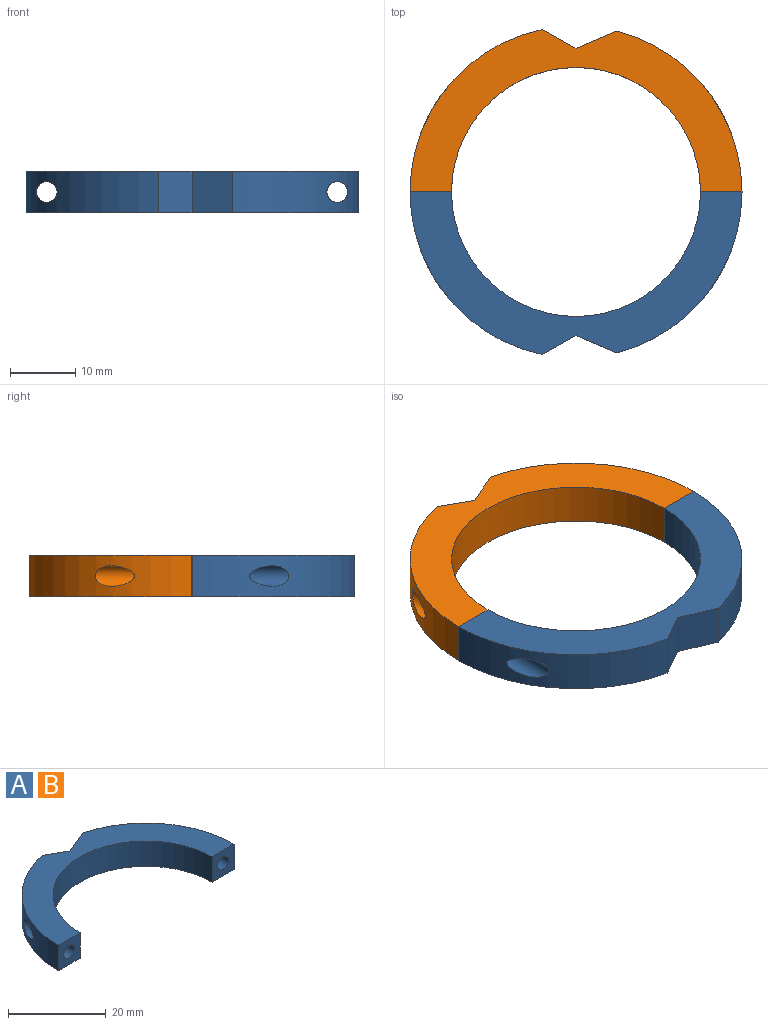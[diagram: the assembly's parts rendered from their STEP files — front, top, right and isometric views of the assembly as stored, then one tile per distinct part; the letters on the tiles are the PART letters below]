
ASSEMBLY  parts=2 mates=1
PART A: 11 faces, bbox 50.8x24.9x6.4 mm
  f0: plane 6.35x6.35mm, normal (0,-1,0), area 32.4mm2, adj f1,f6,f7,f8,f10
  f1: cylinder r=25.4mm len=24.63mm, axis (0,0,-1), area 196.8mm2, adj f0,f2,f7,f8,f10
  f2: plane 6.35x6.22mm, normal (-0.39,0.92,0), area 42.9mm2, adj f1,f3,f7,f8
  f3: plane 6.35x5.18mm, normal (0.49,0.87,0), area 37.7mm2, adj f2,f4,f7,f8
  f4: cylinder r=25.4mm len=24.87mm, axis (0,0,-1), area 203.5mm2, adj f3,f5,f7,f8,f9
  f5: plane 6.35x6.35mm, normal (0,-1,0), area 32.4mm2, adj f4,f6,f7,f8,f9
  f6: cylinder r=19.05mm len=38.1mm, axis (0,0,-1), area 380mm2, adj f0,f5,f7,f8
  f7: plane 50.8x24.87mm, normal (0,0,1), area 422.6mm2, adj f0,f1,f2,f3,f4,f5,f6
  f8: plane 50.8x24.87mm, normal (0,0,-1), area 422.6mm2, adj f0,f1,f2,f3,f4,f5,f6
  f9: cylinder r=1.59mm len=14.81mm, axis (0,-1,0), area 120.4mm2, adj f4,f5
  f10: cylinder r=1.59mm len=14.81mm, axis (0,-1,0), area 120.3mm2, adj f0,f1
PART B: same geometry as A
PLACE A rot(axis=(1,0,0),180deg) t=(22.35,-10.19,17.49)mm
PLACE B t=(22.35,-10.19,11.14)mm
MATE cylindrical B.f9 <-> A.f9  axis (0,-1,0) through (0.13,-10.19,14.32)mm
